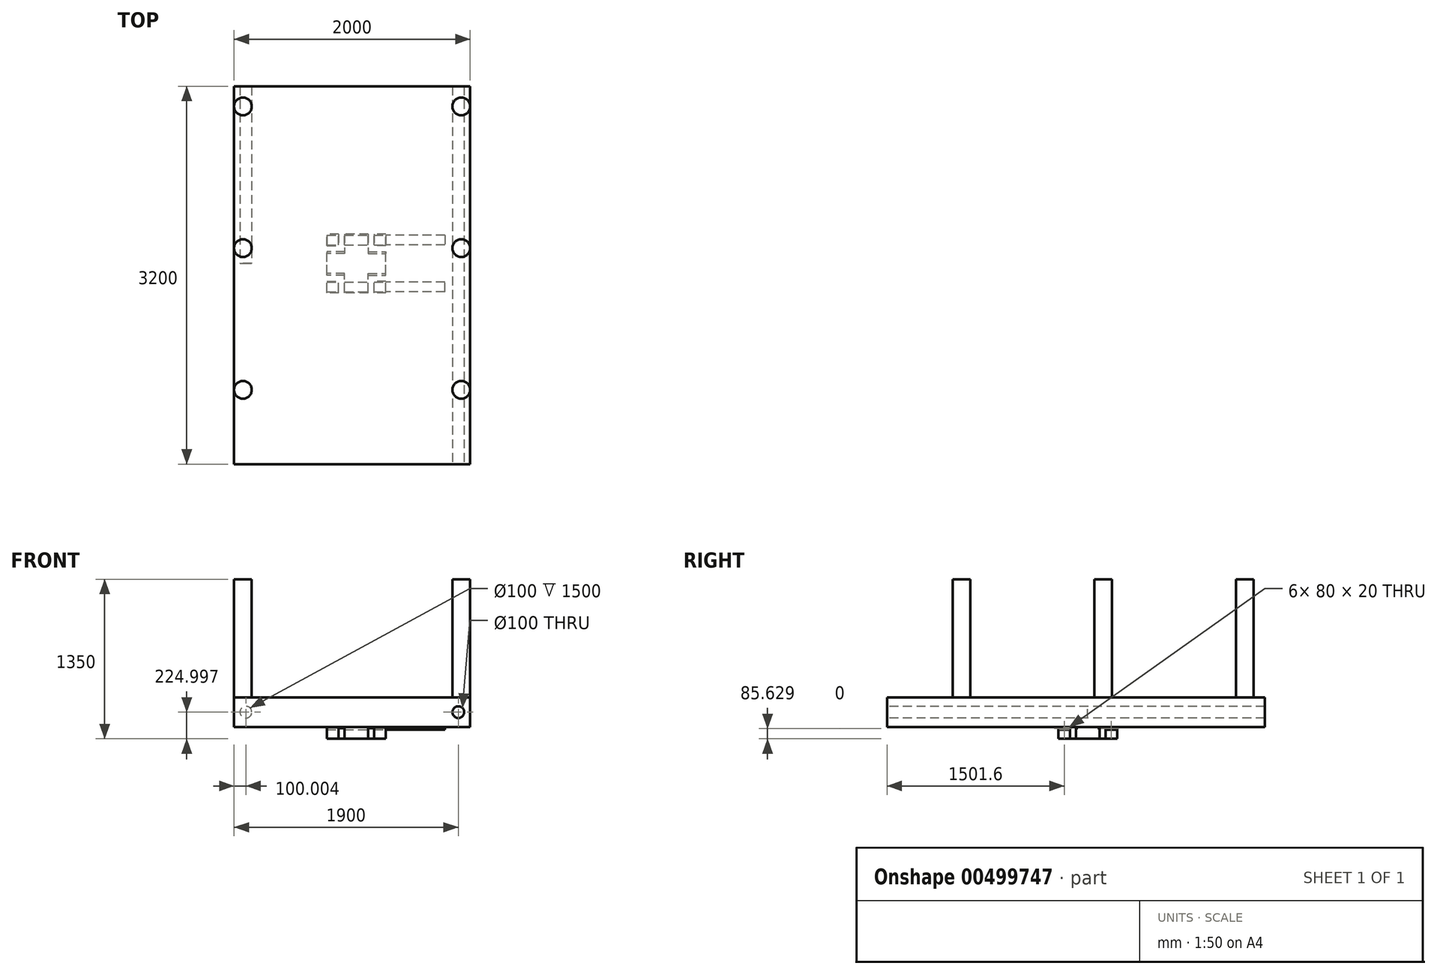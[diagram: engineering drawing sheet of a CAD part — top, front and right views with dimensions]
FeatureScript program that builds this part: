
annotation { "Feature Type Name" : "Feature", "Feature Type Description" : "" }
export const myFeature = defineFeature(function(context is Context, id is Id, definition is map)
    precondition{}
    {
        {
            var Q0;
            Q0=qCreatedBy(makeId("Front.planeOp"),FACE);
            var sketch = newSketch(context, id + "F0", { "sketchPlane" : qUnion([Q0])});
            skLineSegment(sketch, "E0.bottom", {"start": v(-1486.66, -130.42) * mm, "end": v(513.34, -130.42) * mm});
            skLineSegment(sketch, "E0.top", {"start": v(-1486.66, 119.58) * mm, "end": v(513.34, 119.58) * mm});
            skLineSegment(sketch, "E0.left", {"start": v(-1486.66, -130.42) * mm, "end": v(-1486.66, 119.58) * mm});
            skLineSegment(sketch, "E0.right", {"start": v(513.34, -130.42) * mm, "end": v(513.34, 119.58) * mm});
            skCircle(sketch, "E1", {"center": v(-1386.66, -5.42) * mm, "radius": 50 * mm});
            skPoint(sketch, "E1.centerSnap0", {"position": v(-1486.66, -5.42) * mm});
            skLineSegment(sketch, "E2", {"start": v(-486.66, 119.58) * mm, "end": v(-486.66, -130.42) * mm, "construction": true});
            skCircle(sketch, "E3.MirrorC", {"center": v(413.34, -5.42) * mm, "radius": 50 * mm});
            skPoint(sketch, "E4.center.orphan", {"position": v(-100.06, -5.42) * mm});
            skSolve(sketch);
        }
        {
            var Q0;
            Q0=makeQuery(id+"F0.imprint","IMPRINT",FACE,{"disambiguationData":[TD([[makeQuery(id+"F0.imprint","IMPRINT",EDGE,{"derivedFrom":sQuery(id+"F0.wireOp",EDGE,"E0.bottom")}),1.0]])]});
            extrude(context, id + "F1", {"entities" : qUnion([Q0]), "oppositeDirection" : true, "depth" : 3000 * mm, "symmetric" : true});
        }
        {
            var Q0;
            Q0=makeQuery(id+"F1.opExtrude","SWEPT_FACE",FACE,{"disambiguationData":[OSD([sQuery(id+"F0.wireOp",EDGE,"E0.bottom")])]});
            var sketch = newSketch(context, id + "F2", { "sketchPlane" : qUnion([Q0])});
            skLineSegment(sketch, "E5.bottom", {"start": v(-200, 250) * mm, "end": v(-700, 250) * mm});
            skLineSegment(sketch, "E5.top", {"start": v(-200, -250) * mm, "end": v(-700, -250) * mm});
            skLineSegment(sketch, "E5.left", {"start": v(-200, 250) * mm, "end": v(-200, -250) * mm});
            skLineSegment(sketch, "E5.right", {"start": v(-700, 250) * mm, "end": v(-700, -250) * mm});
            skPoint(sketch, "E5.middle", {"position": v(-450, 0) * mm});
            skLineSegment(sketch, "E6.top", {"start": v(-700, 150) * mm, "end": v(-600, 150) * mm});
            skLineSegment(sketch, "E6.right", {"start": v(-600, 250) * mm, "end": v(-600, 150) * mm});
            skLineSegment(sketch, "E7.bottom", {"start": v(-700, 250) * mm, "end": v(-550, 250) * mm});
            skLineSegment(sketch, "E7.top", {"start": v(-700, 100) * mm, "end": v(-550, 100) * mm});
            skLineSegment(sketch, "E7.left", {"start": v(-700, 250) * mm, "end": v(-700, 100) * mm});
            skLineSegment(sketch, "E7.right", {"start": v(-550, 250) * mm, "end": v(-550, 100) * mm});
            skLineSegment(sketch, "E8", {"start": v(-700, 0) * mm, "end": v(-200, 0) * mm, "construction": true});
            skLineSegment(sketch, "E9", {"start": v(-450, 250) * mm, "end": v(-450, -250) * mm, "construction": true});
            skLineSegment(sketch, "E10.MirrorCS", {"start": v(-200, 100) * mm, "end": v(-350, 100) * mm});
            skLineSegment(sketch, "E11.MirrorCS", {"start": v(-200, 150) * mm, "end": v(-300, 150) * mm});
            skLineSegment(sketch, "E12.MirrorCS", {"start": v(-300, 250) * mm, "end": v(-300, 150) * mm});
            skLineSegment(sketch, "E13.MirrorCS", {"start": v(-350, 250) * mm, "end": v(-350, 100) * mm});
            skLineSegment(sketch, "E14.MirrorCS", {"start": v(-700, -100) * mm, "end": v(-550, -100) * mm});
            skLineSegment(sketch, "E15.MirrorCS", {"start": v(-700, -150) * mm, "end": v(-600, -150) * mm});
            skLineSegment(sketch, "E16.MirrorCS", {"start": v(-600, -250) * mm, "end": v(-600, -150) * mm});
            skLineSegment(sketch, "E17.MirrorCS", {"start": v(-550, -250) * mm, "end": v(-550, -100) * mm});
            skLineSegment(sketch, "E18.MirrorCS", {"start": v(-350, -250) * mm, "end": v(-350, -100) * mm});
            skLineSegment(sketch, "E19.MirrorCS", {"start": v(-200, -100) * mm, "end": v(-350, -100) * mm});
            skLineSegment(sketch, "E20.MirrorCS", {"start": v(-200, -150) * mm, "end": v(-300, -150) * mm});
            skLineSegment(sketch, "E21.MirrorCS", {"start": v(-300, -250) * mm, "end": v(-300, -150) * mm});
            skSolve(sketch);
        }
        {
            var Q0;
            {var subQ5=sQuery(id+"F2.wireOp",EDGE,"E7.top");Q0=makeQuery(id+"F2.imprint","IMPRINT",FACE,{"disambiguationData":[TD([[makeQuery(id+"F2.imprint","IMPRINT",EDGE,{"derivedFrom":subQ5}),-1.0]])]});}
            var Q1;
            {var subQ0=sQuery(id+"F2.wireOp",EDGE,"E6.top");Q1=makeQuery(id+"F2.imprint","IMPRINT",FACE,{"disambiguationData":[TD([[makeQuery(id+"F2.imprint","IMPRINT",EDGE,{"derivedFrom":subQ0}),1.0]])]});}
            var Q2;
            {var subQ4=sQuery(id+"F2.wireOp",EDGE,"E11.MirrorCS");Q2=makeQuery(id+"F2.imprint","IMPRINT",FACE,{"disambiguationData":[TD([[makeQuery(id+"F2.imprint","IMPRINT",EDGE,{"derivedFrom":subQ4}),-1.0]])]});}
            var Q3;
            {var subQ4=sQuery(id+"F2.wireOp",EDGE,"E20.MirrorCS");Q3=makeQuery(id+"F2.imprint","IMPRINT",FACE,{"disambiguationData":[TD([[makeQuery(id+"F2.imprint","IMPRINT",EDGE,{"derivedFrom":subQ4}),1.0]])]});}
            var Q4;
            {var subQ4=sQuery(id+"F2.wireOp",EDGE,"E15.MirrorCS");Q4=makeQuery(id+"F2.imprint","IMPRINT",FACE,{"disambiguationData":[TD([[makeQuery(id+"F2.imprint","IMPRINT",EDGE,{"derivedFrom":subQ4}),-1.0]])]});}
            extrude(context, id + "F3", {"entities" : qUnion([Q0, Q1, Q2, Q3, Q4]), "operationType" : NewBodyOperationType.ADD, "depth" : 100 * mm, "offsetDistance" : 25 * mm});
        }
        {
            var Q0;
            {var subQ0=sQuery(id+"F2.wireOp",EDGE,"E5.left");Q0=makeQuery(id+"F3.opExtrude","SWEPT_FACE",FACE,{"disambiguationData":[OSD([subQ0]),TDD([makeQuery(id+"F2.imprint","IMPRINT",EDGE,{"disambiguationData":[TD([[makeQuery(id+"F2.imprint","INTERSECT",VERTEX,{"derivedFrom":[subQ0,sQuery(id+"F2.wireOp",EDGE,"E10.MirrorCS")]}),-1.0]])],"derivedFrom":subQ0})])]});}
            var sketch = newSketch(context, id + "F4", { "sketchPlane" : qUnion([Q0])});
            skLineSegment(sketch, "E22", {"start": v(0, 0) * mm, "end": v(0, -130.42) * mm, "construction": true});
            skLineSegment(sketch, "E23", {"start": v(0, -130.42) * mm, "end": v(0, -230.42) * mm, "construction": true});
            skPoint(sketch, "E24.top.end.orphan", {"position": v(-149.48, -230.47) * mm});
            skLineSegment(sketch, "E25.MirrorCS", {"start": v(238.4, -154.8) * mm, "end": v(158.4, -154.8) * mm});
            skPoint(sketch, "E26.MirrorCS.end.orphan", {"position": v(249.48, -154.8) * mm});
            skPoint(sketch, "E26.MirrorCS.start.orphan", {"position": v(249.48, -134.8) * mm});
            skLineSegment(sketch, "E27", {"start": v(158.4, -134.8) * mm, "end": v(158.4, -154.8) * mm});
            skLineSegment(sketch, "E28", {"start": v(158.4, -154.8) * mm, "end": v(238.4, -154.8) * mm});
            skLineSegment(sketch, "E29", {"start": v(238.4, -154.8) * mm, "end": v(238.4, -134.8) * mm});
            skLineSegment(sketch, "E30.trimOffspring", {"start": v(238.4, -134.8) * mm, "end": v(158.4, -134.8) * mm});
            skPoint(sketch, "E31.orphan", {"position": v(149.48, -154.8) * mm});
            skPoint(sketch, "E32.MirrorCS.start.orphan", {"position": v(149.48, -134.8) * mm});
            skLineSegment(sketch, "E33.MirrorCS", {"start": v(-158.4, -134.8) * mm, "end": v(-158.4, -154.8) * mm});
            skLineSegment(sketch, "E34.MirrorCS", {"start": v(-158.4, -154.8) * mm, "end": v(-238.4, -154.8) * mm});
            skLineSegment(sketch, "E35.MirrorCS", {"start": v(-238.4, -134.8) * mm, "end": v(-158.4, -134.8) * mm});
            skLineSegment(sketch, "E36.MirrorCS", {"start": v(-238.4, -154.8) * mm, "end": v(-238.4, -134.8) * mm});
            skSolve(sketch);
        }
        {
            var Q0;
            Q0 = qSketchRegion(id + "F4", true);
            extrude(context, id + "F5", {"entities" : qUnion([Q0]), "operationType" : NewBodyOperationType.REMOVE, "oppositeDirection" : true, "depth" : 657 * mm});
        }
        {
            var Q0;
            {var subQ0=sQuery(id+"F2.wireOp",EDGE,"E5.left");Q0=makeQuery(id+"F3.opExtrude","SWEPT_FACE",FACE,{"disambiguationData":[OSD([subQ0]),TDD([makeQuery(id+"F2.imprint","IMPRINT",EDGE,{"disambiguationData":[TD([[makeQuery(id+"F2.imprint","INTERSECT",VERTEX,{"derivedFrom":[subQ0,sQuery(id+"F2.wireOp",EDGE,"E10.MirrorCS")]}),-1.0]])],"derivedFrom":subQ0})])]});}
            var sketch = newSketch(context, id + "F6", { "sketchPlane" : qUnion([Q0])});
            skLineSegment(sketch, "E37.bottom", {"start": v(-100, -130.42) * mm, "end": v(-85, -130.42) * mm});
            skLineSegment(sketch, "E37.top", {"start": v(-100, -140.42) * mm, "end": v(-85, -140.42) * mm});
            skLineSegment(sketch, "E37.left", {"start": v(-100, -130.42) * mm, "end": v(-100, -140.42) * mm});
            skLineSegment(sketch, "E37.right", {"start": v(-85, -130.42) * mm, "end": v(-85, -140.42) * mm});
            skLineSegment(sketch, "E38", {"start": v(0, 0) * mm, "end": v(0, -214.09) * mm, "construction": true});
            skPoint(sketch, "E38.endSnap0", {"position": v(0, -130.42) * mm});
            skLineSegment(sketch, "E39.MirrorCS", {"start": v(85, -130.42) * mm, "end": v(85, -140.42) * mm});
            skLineSegment(sketch, "E40.MirrorCS", {"start": v(100, -140.42) * mm, "end": v(85, -140.42) * mm});
            skLineSegment(sketch, "E41.MirrorCS", {"start": v(100, -130.42) * mm, "end": v(85, -130.42) * mm});
            skLineSegment(sketch, "E42.MirrorCS", {"start": v(100, -130.42) * mm, "end": v(100, -140.42) * mm});
            skSolve(sketch);
        }
        {
            var Q0;
            Q0=makeQuery(id+"F6.imprint","IMPRINT",FACE,{"disambiguationData":[TD([[makeQuery(id+"F6.imprint","IMPRINT",EDGE,{"derivedFrom":sQuery(id+"F6.wireOp",EDGE,"E37.bottom")}),-1.0]])]});
            var Q1;
            Q1=makeQuery(id+"F6.imprint","IMPRINT",FACE,{"disambiguationData":[TD([[makeQuery(id+"F6.imprint","IMPRINT",EDGE,{"derivedFrom":sQuery(id+"F6.wireOp",EDGE,"E39.MirrorCS")}),1.0]])]});
            extrude(context, id + "F7", {"entities" : qUnion([Q0, Q1]), "operationType" : NewBodyOperationType.REMOVE, "oppositeDirection" : true, "depth" : 150 * mm});
        }
        {
            var Q0;
            {var subQ0=sQuery(id+"F2.wireOp",EDGE,"E5.right");Q0=makeQuery(id+"F3.opExtrude","SWEPT_FACE",FACE,{"disambiguationData":[OSD([subQ0]),TDD([makeQuery(id+"F2.imprint","IMPRINT",EDGE,{"disambiguationData":[TD([[makeQuery(id+"F2.imprint","INTERSECT",VERTEX,{"derivedFrom":[subQ0,sQuery(id+"F2.wireOp",EDGE,"E14.MirrorCS")]}),1.0]])],"derivedFrom":subQ0})])]});}
            var sketch = newSketch(context, id + "F8", { "sketchPlane" : qUnion([Q0])});
            skLineSegment(sketch, "E43.bottom", {"start": v(-100, -130.42) * mm, "end": v(-85, -130.42) * mm});
            skLineSegment(sketch, "E43.top", {"start": v(-100, -140.42) * mm, "end": v(-85, -140.42) * mm});
            skLineSegment(sketch, "E43.left", {"start": v(-100, -130.42) * mm, "end": v(-100, -140.42) * mm});
            skLineSegment(sketch, "E43.right", {"start": v(-85, -130.42) * mm, "end": v(-85, -140.42) * mm});
            skLineSegment(sketch, "E44", {"start": v(0, 0) * mm, "end": v(0, -230.42) * mm, "construction": true});
            skLineSegment(sketch, "E45.MirrorCS", {"start": v(85, -130.42) * mm, "end": v(85, -140.42) * mm});
            skLineSegment(sketch, "E46.MirrorCS", {"start": v(100, -130.42) * mm, "end": v(85, -130.42) * mm});
            skLineSegment(sketch, "E47.MirrorCS", {"start": v(100, -130.42) * mm, "end": v(100, -140.42) * mm});
            skLineSegment(sketch, "E48.MirrorCS", {"start": v(100, -140.42) * mm, "end": v(85, -140.42) * mm});
            skSolve(sketch);
        }
        {
            var Q0;
            Q0=makeQuery(id+"F8.imprint","IMPRINT",FACE,{"disambiguationData":[TD([[makeQuery(id+"F8.imprint","IMPRINT",EDGE,{"derivedFrom":sQuery(id+"F8.wireOp",EDGE,"E45.MirrorCS")}),1.0]])]});
            var Q1;
            Q1=makeQuery(id+"F8.imprint","IMPRINT",FACE,{"disambiguationData":[TD([[makeQuery(id+"F8.imprint","IMPRINT",EDGE,{"derivedFrom":sQuery(id+"F8.wireOp",EDGE,"E43.bottom")}),1.0]])]});
            extrude(context, id + "F9", {"entities" : qUnion([Q0, Q1]), "operationType" : NewBodyOperationType.REMOVE, "oppositeDirection" : true, "depth" : 150 * mm});
        }
        {
            var Q0;
            Q0=makeQuery(id+"F1.opExtrude","CAP_FACE",FACE,{"disambiguationData":[OSD([sQuery(id+"F0.wireOp",EDGE,"E0.bottom"),sQuery(id+"F0.wireOp",EDGE,"E0.top"),sQuery(id+"F0.wireOp",EDGE,"E0.left"),sQuery(id+"F0.wireOp",EDGE,"E0.right"),sQuery(id+"F0.wireOp",EDGE,"E1"),sQuery(id+"F0.wireOp",EDGE,"E4"),sQuery(id+"F0.wireOp",EDGE,"e370bb45-4be8-4ee9-9ced-df2e9349e00f0.MirrorC"),sQuery(id+"F0.wireOp",EDGE,"E3.MirrorC")])],"isStart":true});
            var sketch = newSketch(context, id + "F10", { "sketchPlane" : qUnion([Q0])});
            skPoint(sketch, "E49.end.orphan", {"position": v(-100.06, -5.42) * mm});
            skLineSegment(sketch, "E50", {"start": v(-1486.66, -5.42) * mm, "end": v(513.34, -5.42) * mm, "construction": true});
            skCircle(sketch, "E51", {"center": v(-1386.66, -5.42) * mm, "radius": 50 * mm});
            skCircle(sketch, "E52", {"center": v(413.34, -5.42) * mm, "radius": 50 * mm});
            skSolve(sketch);
        }
        {
            var Q0;
            Q0=makeQuery(id+"F10.imprint","IMPRINT",FACE,{"disambiguationData":[TD([[makeQuery(id+"F10.imprint","IMPRINT",EDGE,{"derivedFrom":sQuery(id+"F10.wireOp",EDGE,"E51")}),1.0]])]});
            var Q1;
            Q1=makeQuery(id+"F10.imprint","IMPRINT",FACE,{"disambiguationData":[TD([[makeQuery(id+"F10.imprint","IMPRINT",EDGE,{"derivedFrom":sQuery(id+"F10.wireOp",EDGE,"E52")}),-1.0]])]});
            extrude(context, id + "F11", {"entities" : qUnion([Q0, Q1]), "operationType" : NewBodyOperationType.ADD, "oppositeDirection" : true, "depth" : 1500 * mm, "hasSecondDirection" : true, "secondDirectionOppositeDirection" : false, "secondDirectionDepth" : 200 * mm});
        }
        {
            var Q0;
            Q0=makeQuery(id+"F1.opExtrude","SWEPT_FACE",FACE,{"disambiguationData":[OSD([sQuery(id+"F0.wireOp",EDGE,"E0.top")])]});
            var sketch = newSketch(context, id + "F12", { "sketchPlane" : qUnion([Q0])});
            skCircle(sketch, "E53", {"center": v(-1411.66, 1330) * mm, "radius": 75 * mm});
            skLineSegment(sketch, "E54", {"start": v(-486.66, 1500) * mm, "end": v(-486.66, -2202.67) * mm, "construction": true});
            skCircle(sketch, "E55", {"center": v(-1411.66, -1070) * mm, "radius": 75 * mm});
            skCircle(sketch, "E56", {"center": v(-1411.66, 130) * mm, "radius": 75 * mm});
            skCircle(sketch, "E57.MirrorC", {"center": v(438.34, 1330) * mm, "radius": 75 * mm});
            skCircle(sketch, "E58.MirrorC", {"center": v(438.34, 130) * mm, "radius": 75 * mm});
            skCircle(sketch, "E59.MirrorC", {"center": v(438.34, -1070) * mm, "radius": 75 * mm});
            skSolve(sketch);
        }
        {
            var Q0;
            Q0 = qSketchRegion(id + "F12", true);
            extrude(context, id + "F13", {"entities" : qUnion([Q0]), "operationType" : NewBodyOperationType.ADD, "depth" : 1000 * mm});
        }
        {
            var Q0;
            Q0=makeQuery(id+"F4.imprint","IMPRINT",FACE,{"disambiguationData":[TD([[makeQuery(id+"F4.imprint","IMPRINT",EDGE,{"derivedFrom":sQuery(id+"F4.wireOp",EDGE,"E33.MirrorCS")}),-1.0]])]});
            var Q1;
            Q1=makeQuery(id+"F4.imprint","IMPRINT",FACE,{"disambiguationData":[TD([[makeQuery(id+"F4.imprint","IMPRINT",EDGE,{"derivedFrom":sQuery(id+"F4.wireOp",EDGE,"E27")}),1.0]])]});
            extrude(context, id + "F14", {"entities" : qUnion([Q0, Q1]), "operationType" : NewBodyOperationType.ADD, "depth" : 500 * mm});
        }
    });
